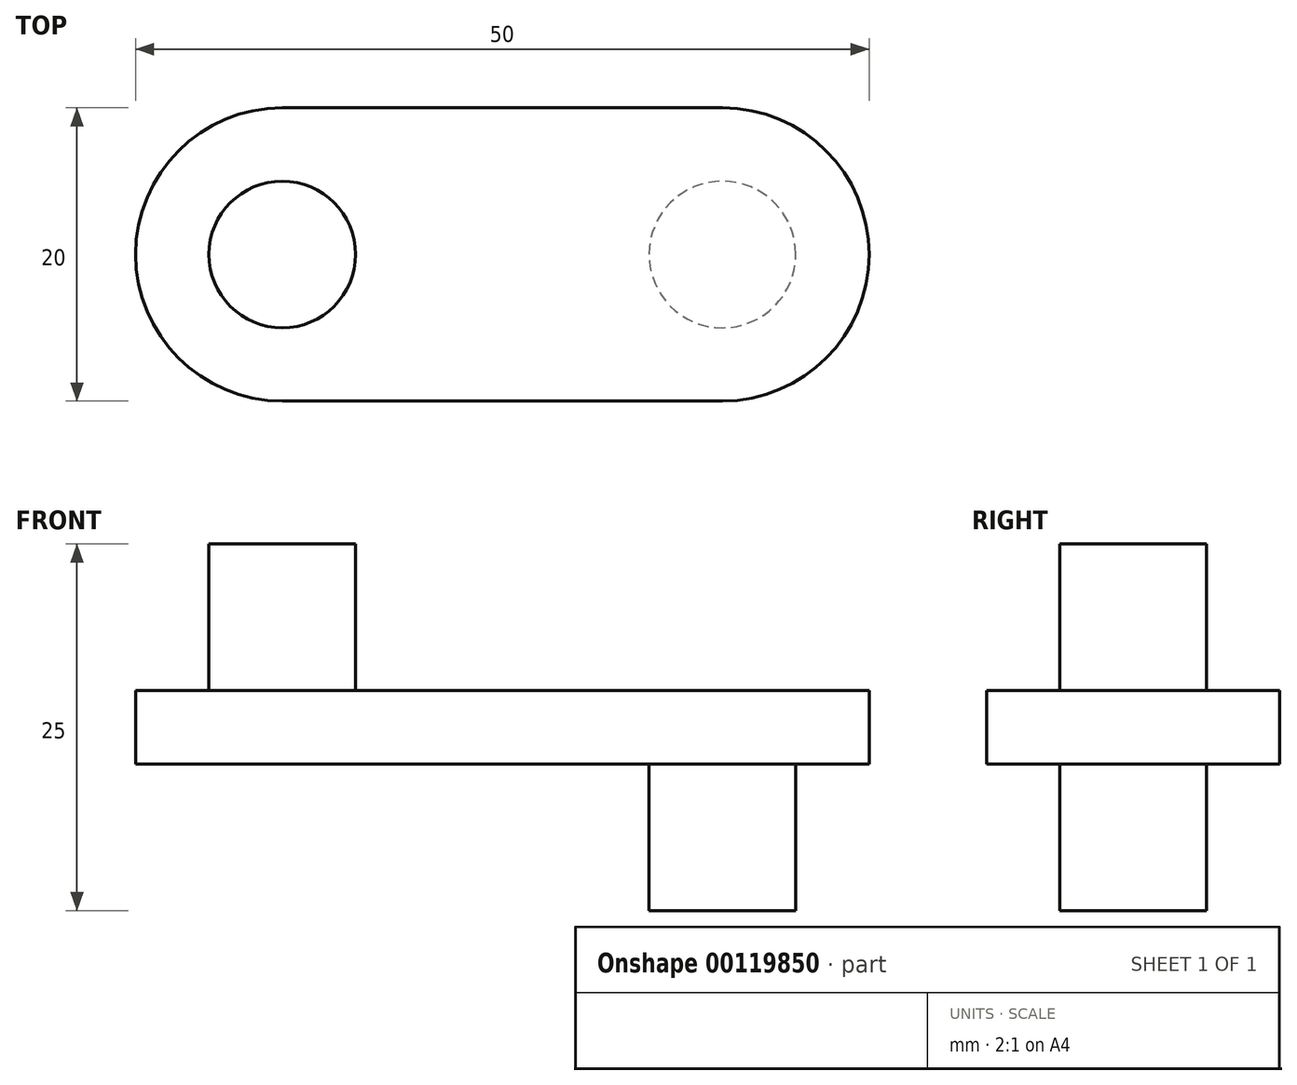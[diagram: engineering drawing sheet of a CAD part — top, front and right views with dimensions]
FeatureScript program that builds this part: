
annotation { "Feature Type Name" : "Feature", "Feature Type Description" : "" }
export const myFeature = defineFeature(function(context is Context, id is Id, definition is map)
    precondition{}
    {
        {
            var Q0;
            Q0=qCreatedBy(makeId("Top.planeOp"),FACE);
            var sketch = newSketch(context, id + "F0", { "sketchPlane" : qUnion([Q0])});
            skCircle(sketch, "E0", {"center": v(0, 0) * mm, "radius": 5 * mm});
            skCircle(sketch, "E1", {"center": v(30, 0) * mm, "radius": 5 * mm});
            skLineSegment(sketch, "E2", {"start": v(0, 10) * mm, "end": v(30, 10) * mm});
            skLineSegment(sketch, "E3", {"start": v(0, -10) * mm, "end": v(30, -10) * mm});
            skArc(sketch, "E4", {"start": v(30, 10) * mm, "mid": v(40, 0) * mm, "end": v(30, -10) * mm});
            skArc(sketch, "E5", {"start": v(0, -10) * mm, "mid": v(-10, 0) * mm, "end": v(0, 10) * mm});
            skSolve(sketch);
        }
        {
            var Q0;
            Q0 = qSketchRegion(id + "F0", true);
            var Q1;
            Q1=makeQuery(id+"F0.imprint","IMPRINT",FACE,{"disambiguationData":[TD([[makeQuery(id+"F0.imprint","IMPRINT",EDGE,{"derivedFrom":sQuery(id+"F0.wireOp",EDGE,"E0")}),1.0]])]});
            var Q2;
            Q2=makeQuery(id+"F0.imprint","IMPRINT",FACE,{"disambiguationData":[TD([[makeQuery(id+"F0.imprint","IMPRINT",EDGE,{"derivedFrom":sQuery(id+"F0.wireOp",EDGE,"E1")}),1.0]])]});
            extrude(context, id + "F1", {"entities" : qUnion([Q0, Q1, Q2]), "depth" : 5 * mm});
        }
        {
            var Q0;
            Q0=makeQuery(id+"F0.imprint","IMPRINT",FACE,{"disambiguationData":[TD([[makeQuery(id+"F0.imprint","IMPRINT",EDGE,{"derivedFrom":sQuery(id+"F0.wireOp",EDGE,"E1")}),1.0]])]});
            extrude(context, id + "F2", {"entities" : qUnion([Q0]), "operationType" : NewBodyOperationType.ADD, "oppositeDirection" : true, "depth" : 10 * mm});
        }
        {
            var Q0;
            Q0=makeQuery(id+"F0.imprint","IMPRINT",FACE,{"disambiguationData":[TD([[makeQuery(id+"F0.imprint","IMPRINT",EDGE,{"derivedFrom":sQuery(id+"F0.wireOp",EDGE,"E0")}),1.0]])]});
            extrude(context, id + "F3", {"entities" : qUnion([Q0]), "operationType" : NewBodyOperationType.ADD, "depth" : 15 * mm});
        }
    });
